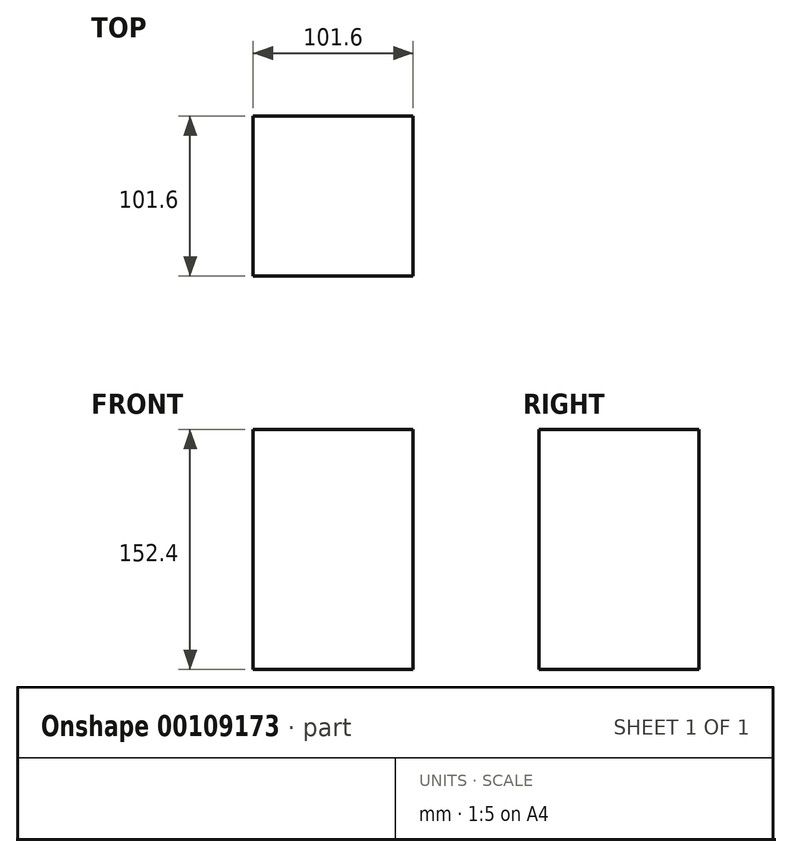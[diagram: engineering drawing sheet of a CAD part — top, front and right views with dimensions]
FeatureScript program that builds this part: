
annotation { "Feature Type Name" : "Feature", "Feature Type Description" : "" }
export const myFeature = defineFeature(function(context is Context, id is Id, definition is map)
    precondition{}
    {
        {
            var Q0;
            Q0=qCreatedBy(makeId("Front.planeOp"),FACE);
            var sketch = newSketch(context, id + "F0", { "sketchPlane" : qUnion([Q0])});
            skLineSegment(sketch, "E0.bottom", {"start": v(50.8, -76.2) * mm, "end": v(-50.8, -76.2) * mm});
            skLineSegment(sketch, "E0.top", {"start": v(50.8, 76.2) * mm, "end": v(-50.8, 76.2) * mm});
            skLineSegment(sketch, "E0.left", {"start": v(50.8, -76.2) * mm, "end": v(50.8, 76.2) * mm});
            skLineSegment(sketch, "E0.right", {"start": v(-50.8, -76.2) * mm, "end": v(-50.8, 76.2) * mm});
            skPoint(sketch, "E0.middle", {"position": v(0, 0) * mm});
            skLineSegment(sketch, "E1", {"start": v(-15.37, 97.83) * mm, "end": v(137.03, 97.83) * mm});
            skSolve(sketch);
        }
        {
            var Q0;
            Q0=makeQuery(id+"F0.imprint","IMPRINT",FACE,{"disambiguationData":[TD([[makeQuery(id+"F0.imprint","IMPRINT",EDGE,{"derivedFrom":sQuery(id+"F0.wireOp",EDGE,"E0.bottom")}),-1.0]])]});
            extrude(context, id + "F1", {"entities" : qUnion([Q0]), "depth" : 101.6 * mm});
        }
    });
